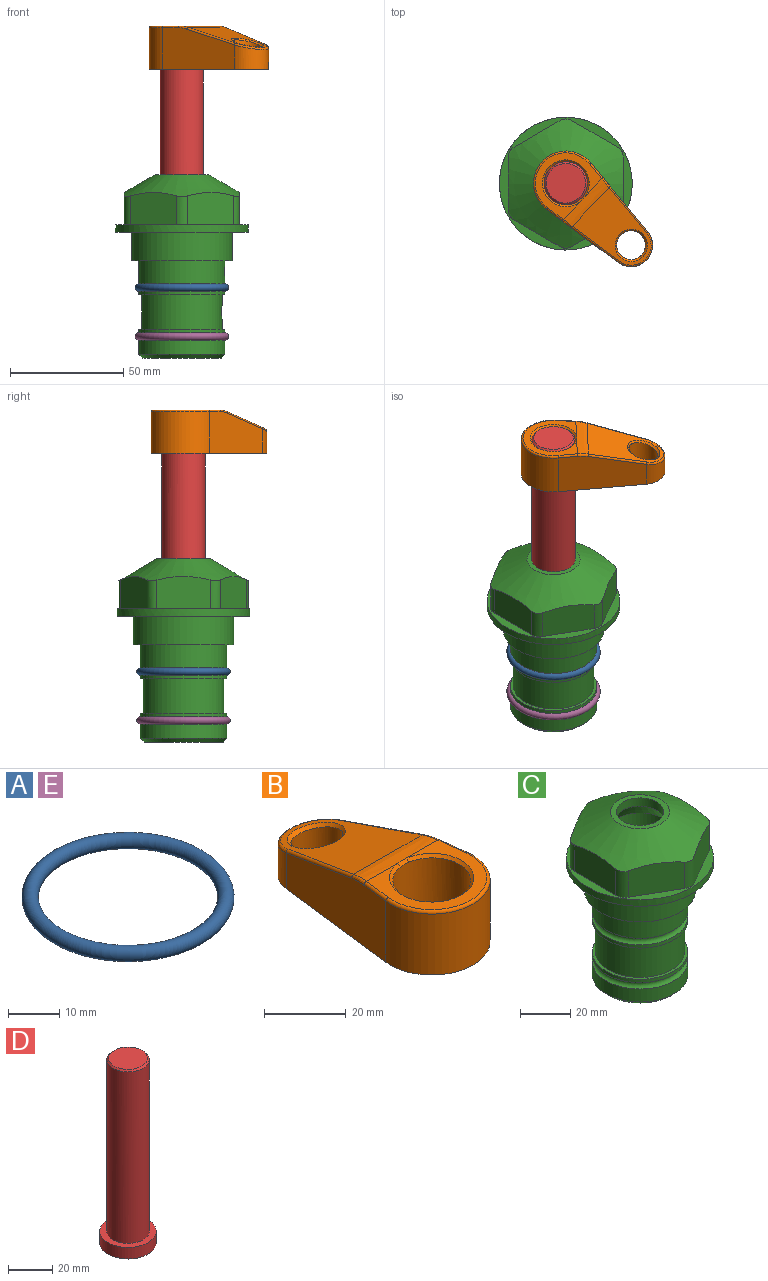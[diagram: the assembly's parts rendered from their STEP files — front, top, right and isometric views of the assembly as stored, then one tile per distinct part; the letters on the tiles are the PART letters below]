
ASSEMBLY  parts=5 mates=4
PART A: 1 faces, bbox 44.7x44.7x3.2 mm
  f0: torus R=19.05mm, axis (0,0,1), area 1193.9mm2
PART B: 31 faces, bbox 31.7x65.5x19.8 mm
  f0: plane 39.12x18.26mm, normal (0.99,0.12,0), area 612.2mm2, adj f1,f4,f7,f11,f13,f15
  f1: cylinder r=9.53mm len=18.91mm, axis (0,0,-1), area 296.1mm2, adj f0,f2,f7,f17
  f2: plane 39.12x18.26mm, normal (-0.99,0.12,0), area 612.2mm2, adj f1,f4,f7,f12,f14,f16
  f3: cylinder r=6.35mm len=12.7mm, axis (0,0,-1), area 362.4mm2, adj f7,f18
  f4: cylinder r=14.29mm len=28.58mm, axis (0,0,-1), area 882.2mm2, adj f0,f2,f7,f10
  f5: cylinder r=9.53mm len=19.05mm, axis (0,0,-1), area 1092.6mm2, adj f7,f19,f20
  f6: plane 26.99x23.69mm, normal (0,0,1), area 216.2mm2, adj f9,f10,f11,f12,f19
  f7: plane 63.5x28.58mm, normal (0,0,-1), area 661.8mm2, adj f0,f1,f2,f3,f4,f5,f22,f23
  f8: plane 33.52x23.6mm, normal (0,0.26,0.97), area 486mm2, adj f9,f15,f16,f17,f18
  f9: cylinder r=19.05mm len=24.72mm, axis (1,0,0), area 120.4mm2, adj f6,f8,f13,f14,f20
  f10: torus R=13.49mm, axis (0,0,1), area 59mm2, adj f4,f6,f11,f12
  f11: cylinder r=0.79mm len=8.67mm, axis (0.12,-0.99,0), area 10.8mm2, adj f0,f6,f10,f13
  f12: cylinder r=0.79mm len=8.67mm, axis (0.12,0.99,0), area 10.8mm2, adj f2,f6,f10,f14
  f13: bspline ~4.95x1.42mm, area 6.1mm2, adj f0,f9,f11,f15
  f14: bspline ~4.95x1.42mm, area 6.1mm2, adj f2,f9,f12,f16
  f15: cylinder r=0.79mm len=25.95mm, axis (0.12,-0.96,0.26), area 32.9mm2, adj f0,f8,f13,f17
  f16: cylinder r=0.79mm len=25.95mm, axis (0.12,0.96,-0.26), area 32.9mm2, adj f2,f8,f14,f17
  f17: bspline ~18.91x8.38mm, area 30mm2, adj f1,f8,f15,f16
  f18: bspline ~14.29x14.29mm, area 48.3mm2, adj f3,f8
  f19: cone r=9.53mm half-angle=45deg, axis (0,0,1), area 66.5mm2, adj f5,f6,f20
  f20: bspline ~3.22x0.96mm, area 3.5mm2, adj f5,f9,f19
  f21: plane 2.75x2.72mm, normal (0,0,-1), area 2.9mm2, adj f23,f25,f28
  f22: plane 23.05x15.88mm, normal (-0.99,-0.12,0), area 323.6mm2, adj f7,f25,f26,f27,f28,f29
  f23: plane 23.05x15.88mm, normal (0.99,-0.12,0), area 323.6mm2, adj f7,f21,f25,f27,f28,f30
  f24: cylinder r=9.53mm len=10.69mm, axis (0,0,-1), area 114.7mm2, adj f7,f27,f29,f30
  f25: cylinder r=12.7mm len=20.59mm, axis (0,0,-1), area 381.1mm2, adj f7,f21,f22,f23,f26,f28
  f26: plane 2.75x2.72mm, normal (0,0,-1), area 2.9mm2, adj f22,f25,f28
  f27: plane 19.72x18.37mm, normal (0,-0.26,-0.97), area 291.8mm2, adj f22,f23,f24,f28,f29,f30
  f28: cylinder r=15.88mm len=19.92mm, axis (1,0,0), area 54.8mm2, adj f21,f22,f23,f25,f26,f27
  f29: cylinder r=1.59mm len=11mm, axis (0,0,-1), area 34.7mm2, adj f7,f22,f24,f27
  f30: cylinder r=1.59mm len=11mm, axis (0,0,-1), area 34.7mm2, adj f7,f23,f24,f27
PART C: 36 faces, bbox 58.7x58.7x81 mm
  f0: cylinder r=17.78mm len=35.56mm, axis (0,0,1), area 1670.8mm2, adj f23,f24,f31
  f1: cylinder r=19.05mm len=38.1mm, axis (0,0,1), area 1191.9mm2, adj f26,f27,f30
  f2: plane 58.66x58.66mm, normal (0,0,-1), area 1150.6mm2, adj f3,f28
  f3: cylinder r=29.33mm len=58.66mm, axis (0,0,-1), area 585.1mm2, adj f2,f4
  f4: plane 58.66x58.66mm, normal (0,0,1), area 475.9mm2, adj f3,f5,f6,f7,f8,f9,f10,f11
  f5: plane 20.32x14.34mm, normal (-0.5,0.87,0), area 324.4mm2, adj f4,f15,f16,f17
  f6: plane 20.32x14.34mm, normal (0.5,0.87,0), area 324.4mm2, adj f4,f14,f15,f17
  f7: plane 23.48x14.34mm, normal (1,0,0), area 324.4mm2, adj f4,f13,f14,f17
  f8: plane 20.32x14.34mm, normal (0.5,-0.87,0), area 324.4mm2, adj f4,f12,f13,f17
  f9: plane 20.32x14.34mm, normal (-0.5,-0.87,0), area 324.4mm2, adj f4,f11,f12,f17
  f10: plane 23.48x14.34mm, normal (-1,0,0), area 324.4mm2, adj f4,f11,f16,f17
  f11: cylinder r=5.08mm len=12.85mm, axis (0,0,-1), area 67.2mm2, adj f4,f9,f10,f17
  f12: cylinder r=5.08mm len=12.85mm, axis (0,0,-1), area 67.2mm2, adj f4,f8,f9,f17
  f13: cylinder r=5.08mm len=12.85mm, axis (0,0,-1), area 67.2mm2, adj f4,f7,f8,f17
  f14: cylinder r=5.08mm len=12.85mm, axis (0,0,-1), area 67.2mm2, adj f4,f6,f7,f17
  f15: cylinder r=5.08mm len=12.85mm, axis (0,0,-1), area 67.2mm2, adj f4,f5,f6,f17
  f16: cylinder r=5.08mm len=12.85mm, axis (0,0,-1), area 67.2mm2, adj f4,f5,f10,f17
  f17: cone r=11.73mm half-angle=60deg, axis (0,0,-1), area 2071.8mm2, adj f5,f6,f7,f8,f9,f10,f11,f12
  f18: plane 23.46x23.46mm, normal (0,0,1), area 147.4mm2, adj f17,f35
  f19: plane 34.93x34.93mm, normal (0,0,-1), area 958mm2, adj f29
  f20: cylinder r=19.05mm len=38.1mm, axis (0,0,1), area 760.1mm2, adj f21,f29
  f21: torus R=19.05mm, axis (0,0,1), area 565.3mm2, adj f20,f22
  f22: cylinder r=19.05mm len=38.1mm, axis (0,0,1), area 190mm2, adj f21,f23
  f23: plane 38.1x38.1mm, normal (0,0,1), area 146.9mm2, adj f0,f22
  f24: plane 38.1x38.1mm, normal (0,0,-1), area 146.9mm2, adj f0,f25
  f25: cylinder r=19.05mm len=38.1mm, axis (0,0,1), area 190mm2, adj f24,f26
  f26: torus R=19.05mm, axis (0,0,1), area 565.3mm2, adj f1,f25
  f27: plane 44.45x44.45mm, normal (0,0,-1), area 411.7mm2, adj f1,f28
  f28: cylinder r=22.23mm len=44.45mm, axis (0,0,1), area 1773.5mm2, adj f2,f27
  f29: cone r=19.05mm half-angle=45deg, axis (0,0,1), area 257.5mm2, adj f19,f20
  f30: cylinder r=3.17mm len=6.75mm, axis (-1,0,0), area 128mm2, adj f1,f33
  f31: cylinder r=3.17mm len=6.35mm, axis (-1,0,0), area 102.5mm2, adj f0,f33
  f32: plane 25.4x25.4mm, normal (0,0,1), area 506.7mm2, adj f33
  f33: cylinder r=12.7mm len=66.42mm, axis (0,0,-1), area 5236.2mm2, adj f30,f31,f32,f34
  f34: cone r=9.53mm half-angle=30deg, axis (0,0,-1), area 443.4mm2, adj f33,f35
  f35: cylinder r=9.53mm len=19.05mm, axis (0,0,-1), area 240.9mm2, adj f18,f34
PART D: 6 faces, bbox 25.4x25.4x101.6 mm
  f0: plane 17.46x17.46mm, normal (0,0,1), area 239.5mm2, adj f5
  f1: plane 25.4x25.4mm, normal (0,0,-1), area 506.7mm2, adj f2
  f2: cylinder r=12.7mm len=25.4mm, axis (0,0,1), area 506.7mm2, adj f1,f3
  f3: plane 25.4x25.4mm, normal (0,0,1), area 221.7mm2, adj f2,f4
  f4: cylinder r=9.53mm len=94.46mm, axis (0,0,1), area 5653mm2, adj f3,f5
  f5: cone r=8.73mm half-angle=45deg, axis (0,0,-1), area 64.4mm2, adj f0,f4
PART E: same geometry as A
PLACE A at identity
PLACE B rot(axis=(0,0,-1),133.5deg) t=(0,0,27.55)mm
PLACE C at identity fixed
PLACE D rot(axis=(0,0,-1),133.5deg) t=(0,0,27.55)mm
PLACE E t=(0,0,-21.59)mm
MATE fastened E.f0 <-> C.f0  axis (0,0,1) through (0,0,-46.1)mm
MATE cylindrical C.f0 <-> D.f2  axis (0,0,1) through (0,0,-50.55)mm
MATE fastened B.f4 <-> D.f2  axis (0,0,1) through (0,0,91.05)mm
MATE fastened A.f0 <-> C.f0  axis (0,0,1) through (0,0,-24.51)mm
